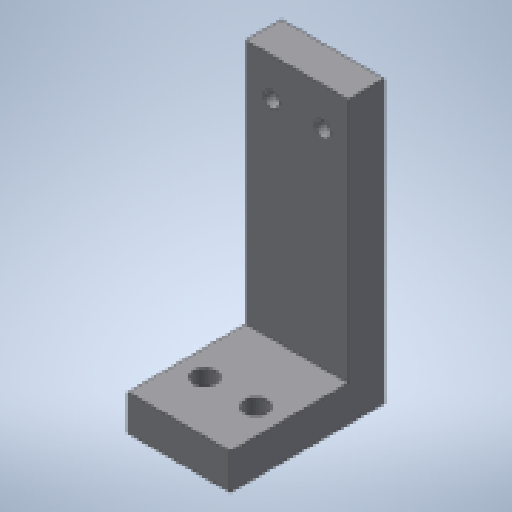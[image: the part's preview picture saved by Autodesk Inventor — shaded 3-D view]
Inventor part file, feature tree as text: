
AUTODESK INVENTOR PART (.ipt)
format: ipt  version: 2023 (Build 270158000, 158)  size: 157,184 bytes
history: native  units: mm
features: extrude x2, sketch x2
ambient origin geometry x8: Origin, YZ Plane, XZ Plane, XY Plane, X Axis, Y Axis, Z Axis, Center Point
bodies: Solid1 (feature_tree)
feature tree (4):
  extrude  "Extrusion1"  Depth=3.0mm
  extrude  "Extrusion2"  Depth=20.0mm
  sketch  "Sketch1"  dims[d0=3.0mm d1=3.0mm]
  sketch  "Sketch2"  dims[d2=10.0mm d3=20.0mm d4=7.5mm d5=7.5mm d6=5.0mm d7=55.0mm d8=7.0mm d9=0.0mm d10=30.0mm d11=4.5mm d12=4.5mm d13=10.0mm d14=5.0mm d15=10.0mm d16=7.0mm d17=0.0mm]
